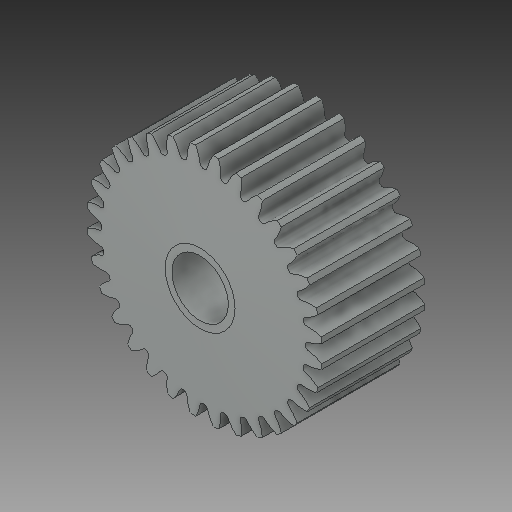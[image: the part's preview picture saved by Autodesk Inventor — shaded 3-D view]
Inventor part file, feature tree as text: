
AUTODESK INVENTOR PART (.ipt)
format: ipt  version: 2017 (Build 210142000, 142)  size: 517,632 bytes
history: native  units: in
note: dims shown in document units (in); Inventor stores cm internally (conversion verified against a paired STEP export)
features: mirror x1
ambient origin geometry x8: Origin, YZ Plane, XZ Plane, XY Plane, X Axis, Y Axis, Z Axis, Center Point
bodies: Solid1 (feature_tree)
feature tree (1):
  mirror  "Mirror1"
